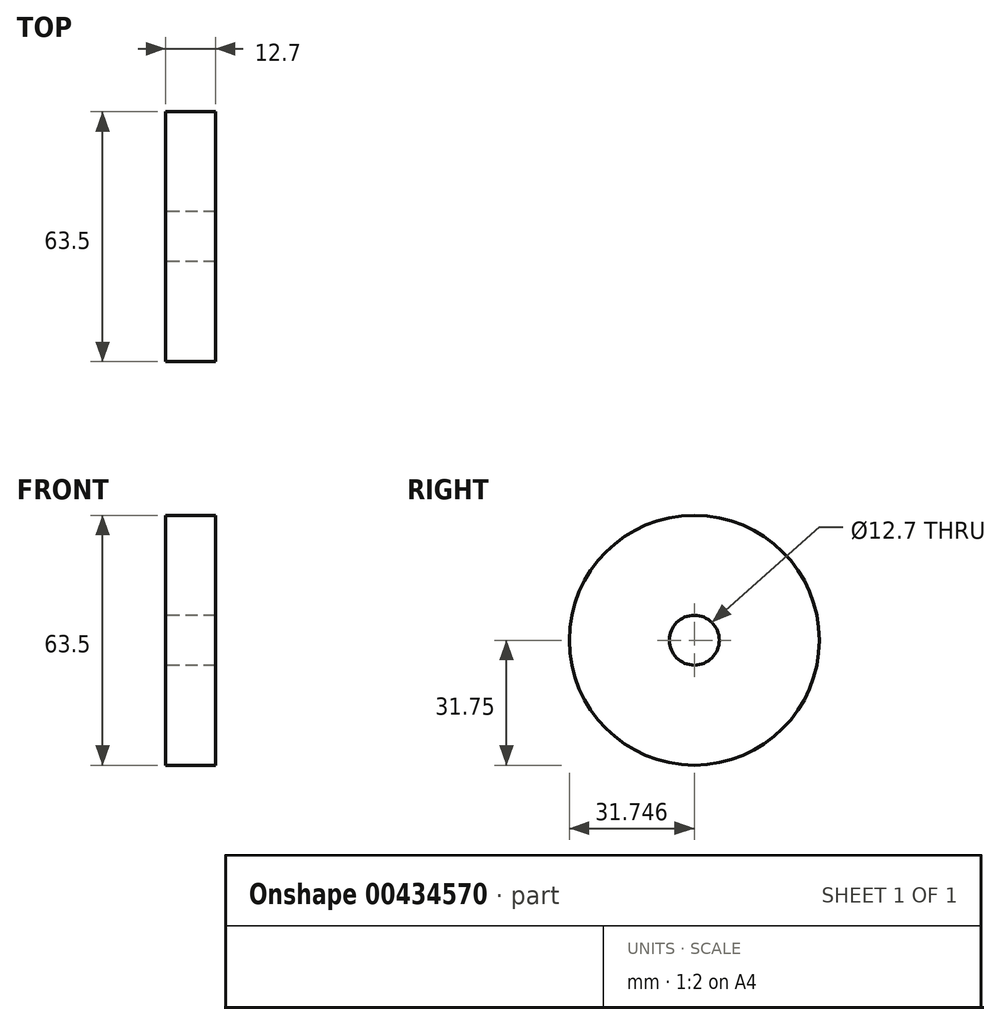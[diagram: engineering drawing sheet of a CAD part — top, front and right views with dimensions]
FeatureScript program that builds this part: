
annotation { "Feature Type Name" : "Feature", "Feature Type Description" : "" }
export const myFeature = defineFeature(function(context is Context, id is Id, definition is map)
    precondition{}
    {
        {
            var Q0;
            Q0=qCreatedBy(makeId("Right.planeOp"),FACE);
            var sketch = newSketch(context, id + "F0", { "sketchPlane" : qUnion([Q0])});
            skCircle(sketch, "E0", {"center": v(-66.1, 34.06) * mm, "radius": 31.75 * mm});
            skCircle(sketch, "E1", {"center": v(-66.1, 34.06) * mm, "radius": 6.35 * mm});
            skSolve(sketch);
        }
        {
            var Q0;
            Q0=makeQuery(id+"F0.imprint","IMPRINT",FACE,{"disambiguationData":[TD([[makeQuery(id+"F0.imprint","IMPRINT",EDGE,{"derivedFrom":sQuery(id+"F0.wireOp",EDGE,"E0")}),1.0]])]});
            extrude(context, id + "F1", {"entities" : qUnion([Q0]), "depth" : 12.7 * mm});
        }
    });
